# Revit family: 1GA-ACF
name_source: partatom
category: Wyposażenie mechaniczne
revit_build: Autodesk Revit 2015 (Build: 20160512_1515(x64)
units: mm (PartAtom-declared; Revit-internal decimal feet)

## types (1)
- GA-ACF S
    Autor = www.archispace.pl
    Ciśnienie akustyczne w odległości 5 metrów = 53 dB (A)
    Ciśnienie gazu zasilającego (LPG G30/G31) = 32 - 42 mbar
    Ciśnienie gazu zasilającego (gaz ziemny G20) = 17 - 23 mbar
    Dokumentacja techniczna = http://www.gazuno.pl
    Głębokość = 1230 mm  [stored 4.03543 ft]
    IP = X5D
    Ilość wody w urządzeniu = 3.0 L
    Klasyfikacja obciążenia = Inne
    Maksymalne ciśnienie robocze = 4 pasek
    Materiał obudowa 1 = Robur_CashmereGrey
    Materiał obudowa 2 = Robur_Czarny
    Materiał podstawa = Robur_Stal
    Max. przepływ wody lodowej = 0.889 L/s
    Max. temperatura powietrza zewnętrznego = 45 °C
    Max. temperatura wody na wejściu do urządzenia = 45 °C
    Min. przepływ wody lodowej = 0.694 L/s
    Min. temperatura powietrza zewnętrznego = 0 °C
    Min. temperatura wody na wejściu do urządzenia = 8 °C
    Min. temperatura wody na wyjściu z urządzenia = 3 °C
    Moc elektryczna = 870 W
    Model = GA-ACF S
    Napięcie zasilania = 230 V
    Nominalna moc grzewcza palnika = 25300 W
    Nominalna temperatura powietrza zewnętrznego = 35 °C
    Nominalna temperatura wody na wyjściu z urządzenia = 7 °C
    Nominalny przepływ wody lodowej = 0.769 L/s
    Obciążenie pozorne = 870 VA
    Opis = Gazowa absorpcyjna wytwornica wody lodowej
    Producent = Robur
    Rzeczywista moc grzewcza palnika = 25000 W
    Spadek ciśnienia wody lodowej przy nominalnym przepływie = 0.29 pasek
    Szerokość = 850 mm  [stored 2.78871 ft]
    URL = www.gazuno.pl
    Waga = 360.00 kg
    Współczynnik mocy = 1
    Wysokość = 1545 mm

note: [stored X ft] marks values corroborated as IEEE doubles in the binary element streams (Revit-internal decimal feet)
